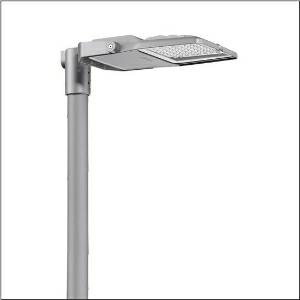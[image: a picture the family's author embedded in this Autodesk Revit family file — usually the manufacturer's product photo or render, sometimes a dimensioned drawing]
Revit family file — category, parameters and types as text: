
# Revit family: floodlight_fl_21_mini___pl64_5xa7775d2e3a_010e
name_source: partatom
category: Lighting Fixtures
units: mm (PartAtom-declared; Revit-internal decimal feet)

## family parameters
Cut with Voids When Loaded = No
Host = Face
Light Source = No
Part Type = Normal
Room Calculation Point = No
Round Connector Dimension = Use Diameter
Shared = No

## types (1)
- --- (1 x LED, 17220 lm, 142.9 W, 3000K)
    Apparent Load = 143 VA
    CIE Flux Codes = 28 80 98 100 100
    Color Rendering = 70
    Color Temperature = 3000K
    Default Elevation = 1800 mm
    Description = Floodlight FL 21 mini, floodlight, primary light control with lens, of PMMA, primary optical cover: protective disc, of toughened safety glass, transparent, light distribution: PL64, light emission: direct distribution, installation type: surface-mounted, LED, High Power LED, rated luminous flux: 17.220lm, luminous efficacy: 121lm/W, light colour: 730, colour temperature: 3000K, control gear: Smart Interface (Zhaga), control: flexible luminous flux parameterisation, time-dependent luminous flux control, constant luminous flux control, overheat protection, pre-setting: logarithmic dimming characteristic, with terminal, 6-pole, mains connection: 220..240V, AC, 50/60Hz, start of lifetime: 143W, end of service life: 151W, reduction: 63W, luminaire housing, of diecast aluminium, powder-coated, Siteco® metallic grey (DB 702S), corrosivity category C5 mid according to DIN EN ISO 12944, suitable for swimming pools, chlorine-resistant, sealing non-destructively replaceable, please order mast flange separately, mast bracket, of steel, galvanised, powder-coated, Siteco® metallic grey (DB 702S), Smart Interface above, protection rating (complete): IP66, insulation class (complete): insulation class II (safety insulation), certification: CE, ENEC, VDE, protection symbol: D, impact resistance: IK08, permissible operating ambient temperature: -40..+40°C, permissible operating ambient temperature for outdoor applications: -40..+50°C, standard: DIN EN 12944, LABS conformity tested according to VDMA 24364:2018-05, packaging unit: 1 piece

Light Distribution: PL64
    Height = 70 mm
    Lamp = 1 x LED
    Lamp Light Flux = 17220 lm
    Lamp Power = 142.9 W
    Lamp count = 1
    Length = 485 mm
    Luminous efficacy = 121 lm/W
    Manufacturer = Siteco
    ModVariant = No
    Model = 5XA7775D2E3A
    Number of Poles = 1
    OnlyDefault = Yes
    Power Factor = 1
    Product Name = Floodlight FL 21 mini | PL64
    Product group = floodlight | pylon annexe
    ProductGroupID = 6200
    Protection Class = Protection class II
    Protection Degree = IP 66
    RLX_Detail_Level = 1
    RLX_Emergency_Light_Flux = 0 lm
    RLX_Emergency_Type = 0
    RLX_Emergency_Type_DB = No
    RlxData = <blob elided: 101433 chars, md5=a1176506>
    Socket = socket
    Standby Power = 0 W
    System Light Flux = 17220 lm
    System Power = 143 W
    Type Comments = factory setting: luminous flux: 100 % | dim-lin: 254 | 730 mA
    Type Image = l_1007125.jpg
    URL = http://relux.com
    VarID = @adj_165276
    Voltage = 0 V
    Weight = 0.00 kg
    Width = 337 mm

## geometry (parser evidence)
native form markers: Blend x4, Sweep x13
no freeform markers — native parametric forms only
